# Revit family: 3270 Björk_Centrefeed paper towel dispenser
name_source: partatom
category: Furniture Systems
revit_build: Autodesk Revit 2018 (Build: 20170223_1515(x64)
units: mm (PartAtom-declared; Revit-internal decimal feet)

## family parameters
Always vertical = Yes
Cut with Voids When Loaded = No
Host = Wall
Part Type = Normal
Room Calculation Point = No
Round Connector Dimension = Use Diameter
Shared = No

## types (6) — shared parameters
Metal Component = Stainless Steel, Brushed
Surface Bottom = WHITE
Surface Front = WHITE

## per-type parameters (varying)
| type | Description | Manufacturer | URL |
| OSLO |  |  |  |
| BIANCO MALE |  |  |  |
| BIRK |  |  |  |
| GEO WHITE |  |  |  |
| GRIGIO LONDRA |  |  |  |
| NEGRO INGO | Centrefeed paper towel dispenser | Dan Dryer A/S | http://www.dandryer.com |

note: column(s) folded — value = type name in every type: Surface Top

## geometry (parser evidence)
native form markers: Sweep x27
no freeform markers — native parametric forms only
